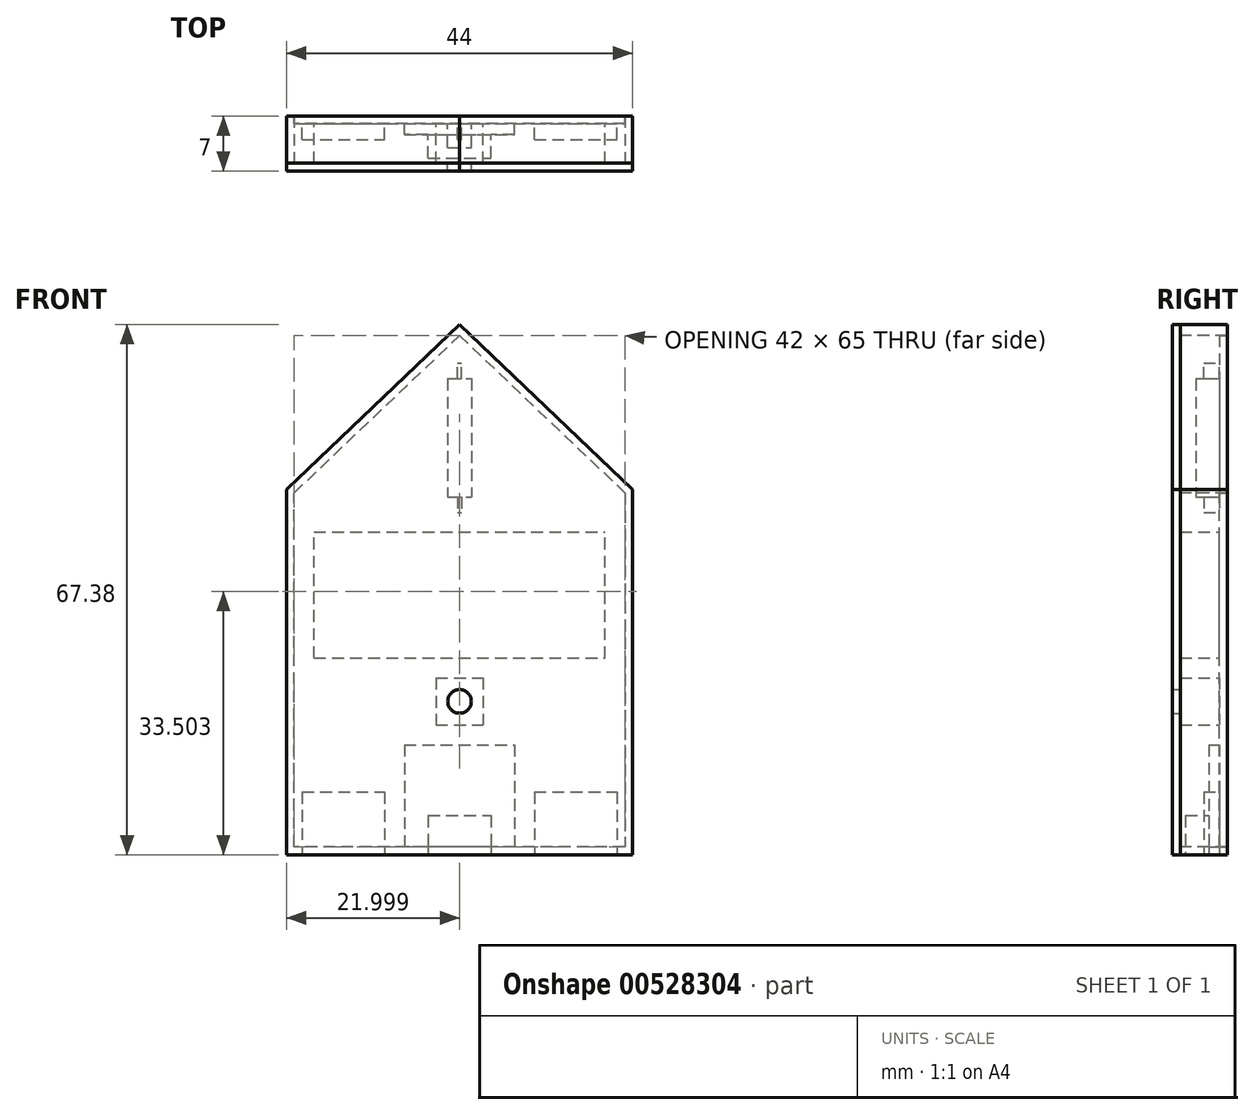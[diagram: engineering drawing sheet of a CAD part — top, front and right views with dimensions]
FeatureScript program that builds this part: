
annotation { "Feature Type Name" : "Feature", "Feature Type Description" : "" }
export const myFeature = defineFeature(function(context is Context, id is Id, definition is map)
    precondition{}
    {
        {
            var Q0;
            Q0=qCreatedBy(makeId("Front.planeOp"),FACE);
            var sketch = newSketch(context, id + "F0", { "sketchPlane" : qUnion([Q0])});
            skLineSegment(sketch, "E0", {"start": v(0.06, 2.74) * mm, "end": v(0.06, 47.74) * mm});
            skLineSegment(sketch, "E1", {"start": v(0.06, 47.74) * mm, "end": v(21.06, 67.74) * mm});
            skLineSegment(sketch, "E2", {"start": v(21.06, 67.74) * mm, "end": v(42.06, 47.74) * mm});
            skLineSegment(sketch, "E3", {"start": v(42.06, 47.74) * mm, "end": v(42.06, 2.74) * mm});
            skLineSegment(sketch, "E4", {"start": v(42.06, 2.74) * mm, "end": v(0.06, 2.74) * mm});
            skLineSegment(sketch, "E5", {"start": v(0.06, 47.74) * mm, "end": v(42.06, 47.74) * mm, "construction": true});
            skLineSegment(sketch, "E6", {"start": v(21.06, 67.74) * mm, "end": v(21.06, 47.74) * mm, "construction": true});
            skSolve(sketch);
        }
        {
            var Q0;
            Q0 = qSketchRegion(id + "F0", true);
            extrude(context, id + "F1", {"entities" : qUnion([Q0]), "depth" : 1 * mm, "offsetDistance" : 25 * mm});
        }
        {
            var Q0;
            Q0=makeQuery(id+"F1.opExtrude","CAP_FACE",FACE,{"disambiguationData":[OSD([sQuery(id+"F0.wireOp",EDGE,"E0"),sQuery(id+"F0.wireOp",EDGE,"E1"),sQuery(id+"F0.wireOp",EDGE,"E2"),sQuery(id+"F0.wireOp",EDGE,"E3"),sQuery(id+"F0.wireOp",EDGE,"E4")])],"isStart":false});
            var sketch = newSketch(context, id + "F2", { "sketchPlane" : qUnion([Q0])});
            skLineSegment(sketch, "E7.bottom", {"start": v(14.06, 15.74) * mm, "end": v(28.06, 15.74) * mm});
            skLineSegment(sketch, "E7.top", {"start": v(14.06, 2.74) * mm, "end": v(28.06, 2.74) * mm});
            skLineSegment(sketch, "E7.left", {"start": v(14.06, 15.74) * mm, "end": v(14.06, 2.74) * mm});
            skLineSegment(sketch, "E7.right", {"start": v(28.06, 15.74) * mm, "end": v(28.06, 2.74) * mm});
            skLineSegment(sketch, "E8", {"start": v(21.06, 15.74) * mm, "end": v(21.06, 2.74) * mm, "construction": true});
            skSolve(sketch);
        }
        {
            var Q0;
            Q0 = qSketchRegion(id + "F2", true);
            extrude(context, id + "F3", {"entities" : qUnion([Q0]), "depth" : 1.34 * mm, "offsetDistance" : 25 * mm});
        }
        {
            var Q0;
            Q0=makeQuery(id+"F3.opExtrude","CAP_FACE",FACE,{"disambiguationData":[OSD([sQuery(id+"F2.wireOp",EDGE,"E7.bottom"),sQuery(id+"F2.wireOp",EDGE,"E7.top"),sQuery(id+"F2.wireOp",EDGE,"E7.left"),sQuery(id+"F2.wireOp",EDGE,"E7.right")])],"isStart":false});
            var sketch = newSketch(context, id + "F4", { "sketchPlane" : qUnion([Q0])});
            skLineSegment(sketch, "E9.bottom", {"start": v(17.06, 6.74) * mm, "end": v(25.06, 6.74) * mm});
            skLineSegment(sketch, "E9.top", {"start": v(17.06, 1.74) * mm, "end": v(25.06, 1.74) * mm});
            skLineSegment(sketch, "E9.left", {"start": v(17.06, 6.74) * mm, "end": v(17.06, 1.74) * mm});
            skLineSegment(sketch, "E9.right", {"start": v(25.06, 6.74) * mm, "end": v(25.06, 1.74) * mm});
            skLineSegment(sketch, "E10", {"start": v(21.06, 6.74) * mm, "end": v(21.06, 1.74) * mm, "construction": true});
            skSolve(sketch);
        }
        {
            var Q0;
            Q0 = qSketchRegion(id + "F4", true);
            extrude(context, id + "F5", {"entities" : qUnion([Q0]), "operationType" : NewBodyOperationType.ADD, "depth" : 3 * mm, "offsetDistance" : 25 * mm});
        }
        {
            var Q0;
            Q0=makeQuery(id+"F2.imprint","IMPRINT",FACE,{"disambiguationData":[TD([[makeQuery(id+"F2.imprint","IMPRINT",EDGE,{"derivedFrom":sQuery(id+"F2.wireOp",EDGE,"E7.bottom")}),1.0]])]});
            var sketch = newSketch(context, id + "F6", { "sketchPlane" : qUnion([Q0])});
            skLineSegment(sketch, "E11.bottom", {"start": v(1.06, 9.74) * mm, "end": v(11.56, 9.74) * mm});
            skLineSegment(sketch, "E11.top", {"start": v(1.06, 1.74) * mm, "end": v(11.56, 1.74) * mm});
            skLineSegment(sketch, "E11.left", {"start": v(1.06, 9.74) * mm, "end": v(1.06, 1.74) * mm});
            skLineSegment(sketch, "E11.right", {"start": v(11.56, 9.74) * mm, "end": v(11.56, 1.74) * mm});
            skLineSegment(sketch, "E12.bottom", {"start": v(30.56, 9.74) * mm, "end": v(41.06, 9.74) * mm});
            skLineSegment(sketch, "E12.top", {"start": v(30.56, 1.74) * mm, "end": v(41.06, 1.74) * mm});
            skLineSegment(sketch, "E12.left", {"start": v(30.56, 9.74) * mm, "end": v(30.56, 1.74) * mm});
            skLineSegment(sketch, "E12.right", {"start": v(41.06, 9.74) * mm, "end": v(41.06, 1.74) * mm});
            skSolve(sketch);
        }
        {
            var Q0;
            Q0 = qSketchRegion(id + "F6", true);
            extrude(context, id + "F7", {"entities" : qUnion([Q0]), "depth" : 2 * mm, "offsetDistance" : 25 * mm});
        }
        {
            var Q0;
            Q0=makeQuery(id+"F2.imprint","IMPRINT",FACE,{"disambiguationData":[TD([[makeQuery(id+"F2.imprint","IMPRINT",EDGE,{"derivedFrom":sQuery(id+"F2.wireOp",EDGE,"E7.bottom")}),1.0]])]});
            var sketch = newSketch(context, id + "F8", { "sketchPlane" : qUnion([Q0])});
            skLineSegment(sketch, "E13.bottom", {"start": v(18.06, 24.24) * mm, "end": v(24.06, 24.24) * mm});
            skLineSegment(sketch, "E13.top", {"start": v(18.06, 18.24) * mm, "end": v(24.06, 18.24) * mm});
            skLineSegment(sketch, "E13.left", {"start": v(18.06, 24.24) * mm, "end": v(18.06, 18.24) * mm});
            skLineSegment(sketch, "E13.right", {"start": v(24.06, 24.24) * mm, "end": v(24.06, 18.24) * mm});
            skLineSegment(sketch, "E14", {"start": v(21.06, 24.24) * mm, "end": v(21.06, 18.24) * mm, "construction": true});
            skSolve(sketch);
        }
        {
            var Q0;
            Q0 = qSketchRegion(id + "F8", true);
            extrude(context, id + "F9", {"entities" : qUnion([Q0]), "depth" : 5 * mm, "offsetDistance" : 25 * mm});
        }
        {
            var Q0;
            Q0=makeQuery(id+"F9.opExtrude","CAP_FACE",FACE,{"disambiguationData":[OSD([sQuery(id+"F8.wireOp",EDGE,"E13.bottom"),sQuery(id+"F8.wireOp",EDGE,"E13.top"),sQuery(id+"F8.wireOp",EDGE,"E13.left"),sQuery(id+"F8.wireOp",EDGE,"E13.right")])],"isStart":false});
            var sketch = newSketch(context, id + "F10", { "sketchPlane" : qUnion([Q0])});
            skCircle(sketch, "E15", {"center": v(21.06, 21.24) * mm, "radius": 1.5 * mm});
            skLineSegment(sketch, "E16", {"start": v(18.06, 24.24) * mm, "end": v(24.06, 18.24) * mm, "construction": true});
            skLineSegment(sketch, "E17", {"start": v(24.06, 24.24) * mm, "end": v(18.06, 18.24) * mm, "construction": true});
            skSolve(sketch);
        }
        {
            var Q0;
            Q0 = qSketchRegion(id + "F10", true);
            extrude(context, id + "F11", {"entities" : qUnion([Q0]), "operationType" : NewBodyOperationType.ADD, "depth" : 1 * mm, "offsetDistance" : 25 * mm});
        }
        {
            var Q0;
            Q0=makeQuery(id+"F2.imprint","IMPRINT",FACE,{"disambiguationData":[TD([[makeQuery(id+"F2.imprint","IMPRINT",EDGE,{"derivedFrom":sQuery(id+"F2.wireOp",EDGE,"E7.bottom")}),1.0]])]});
            var sketch = newSketch(context, id + "F12", { "sketchPlane" : qUnion([Q0])});
            skLineSegment(sketch, "E18.bottom", {"start": v(2.56, 26.74) * mm, "end": v(39.56, 26.74) * mm});
            skLineSegment(sketch, "E18.top", {"start": v(2.56, 42.74) * mm, "end": v(39.56, 42.74) * mm});
            skLineSegment(sketch, "E18.left", {"start": v(2.56, 26.74) * mm, "end": v(2.56, 42.74) * mm});
            skLineSegment(sketch, "E18.right", {"start": v(39.56, 26.74) * mm, "end": v(39.56, 42.74) * mm});
            skLineSegment(sketch, "E19", {"start": v(21.06, 26.74) * mm, "end": v(21.06, 42.74) * mm, "construction": true});
            skSolve(sketch);
        }
        {
            var Q0;
            Q0 = qSketchRegion(id + "F12", true);
            extrude(context, id + "F13", {"entities" : qUnion([Q0]), "depth" : 5 * mm, "offsetDistance" : 25 * mm});
        }
        {
            var Q0;
            Q0=makeQuery(id+"F2.imprint","IMPRINT",FACE,{"disambiguationData":[TD([[makeQuery(id+"F2.imprint","IMPRINT",EDGE,{"derivedFrom":sQuery(id+"F2.wireOp",EDGE,"E7.bottom")}),1.0]])]});
            var sketch = newSketch(context, id + "F14", { "sketchPlane" : qUnion([Q0])});
            skLineSegment(sketch, "E20.bottom", {"start": v(19.56, 62.24) * mm, "end": v(22.56, 62.24) * mm});
            skLineSegment(sketch, "E20.top", {"start": v(19.56, 47.24) * mm, "end": v(22.56, 47.24) * mm});
            skLineSegment(sketch, "E20.left", {"start": v(19.56, 62.24) * mm, "end": v(19.56, 47.24) * mm});
            skLineSegment(sketch, "E20.right", {"start": v(22.56, 62.24) * mm, "end": v(22.56, 47.24) * mm});
            skPoint(sketch, "E21", {"position": v(21.06, 62.24) * mm});
            skSolve(sketch);
        }
        {
            var Q0;
            Q0 = qSketchRegion(id + "F14", true);
            extrude(context, id + "F15", {"entities" : qUnion([Q0]), "depth" : 3 * mm, "offsetDistance" : 25 * mm});
        }
        {
            var Q0;
            Q0=makeQuery(id+"F2.imprint","IMPRINT",FACE,{"disambiguationData":[TD([[makeQuery(id+"F2.imprint","IMPRINT",EDGE,{"derivedFrom":sQuery(id+"F2.wireOp",EDGE,"E7.bottom")}),1.0]])]});
            var sketch = newSketch(context, id + "F16", { "sketchPlane" : qUnion([Q0])});
            skLineSegment(sketch, "E22.bottom", {"start": v(20.8, 47.24) * mm, "end": v(21.3, 47.24) * mm});
            skLineSegment(sketch, "E22.top", {"start": v(20.8, 45.24) * mm, "end": v(21.3, 45.24) * mm});
            skLineSegment(sketch, "E22.left", {"start": v(20.8, 47.24) * mm, "end": v(20.8, 45.24) * mm});
            skLineSegment(sketch, "E22.right", {"start": v(21.3, 47.24) * mm, "end": v(21.3, 45.24) * mm});
            skLineSegment(sketch, "E23.bottom", {"start": v(20.8, 62.24) * mm, "end": v(21.3, 62.24) * mm});
            skLineSegment(sketch, "E23.top", {"start": v(20.8, 64.24) * mm, "end": v(21.3, 64.24) * mm});
            skLineSegment(sketch, "E23.left", {"start": v(20.8, 62.24) * mm, "end": v(20.8, 64.24) * mm});
            skLineSegment(sketch, "E23.right", {"start": v(21.3, 62.24) * mm, "end": v(21.3, 64.24) * mm});
            skPoint(sketch, "E24", {"position": v(21.06, 62.24) * mm});
            skSolve(sketch);
        }
        {
            var Q0;
            Q0 = qSketchRegion(id + "F16", true);
            extrude(context, id + "F17", {"entities" : qUnion([Q0]), "depth" : 2 * mm, "offsetDistance" : 25 * mm});
        }
        {
            var Q0;
            Q0=makeQuery(id+"F13.opExtrude","CAP_FACE",FACE,{"disambiguationData":[OSD([sQuery(id+"F12.wireOp",EDGE,"E18.bottom"),sQuery(id+"F12.wireOp",EDGE,"E18.top"),sQuery(id+"F12.wireOp",EDGE,"E18.left"),sQuery(id+"F12.wireOp",EDGE,"E18.right")])],"isStart":false});
            var sketch = newSketch(context, id + "F18", { "sketchPlane" : qUnion([Q0])});
            skSolve(sketch);
        }
        {
            var Q0;
            Q0=makeQuery(id+"F18.imprint","IMPRINT",FACE,{"disambiguationData":[TD([[makeQuery(id+"F18.imprint","IMPRINT",EDGE,{"derivedFrom":makeQuery(id+"F13.opExtrude","CAP_EDGE",EDGE,{"disambiguationData":[OSD([sQuery(id+"F12.wireOp",EDGE,"E18.bottom")])],"isStart":false})}),1.0]])]});
            var sketch = newSketch(context, id + "F19", { "sketchPlane" : qUnion([Q0])});
            skLineSegment(sketch, "E25.0", {"start": v(43.06, 1.74) * mm, "end": v(43.06, 48.17) * mm});
            skLineSegment(sketch, "E25.1", {"start": v(-0.94, 1.74) * mm, "end": v(43.06, 1.74) * mm});
            skLineSegment(sketch, "E25.2", {"start": v(43.06, 48.17) * mm, "end": v(21.06, 69.12) * mm});
            skLineSegment(sketch, "E25.3", {"start": v(21.06, 69.12) * mm, "end": v(-0.94, 48.17) * mm});
            skLineSegment(sketch, "E25.4", {"start": v(-0.94, 48.17) * mm, "end": v(-0.94, 1.74) * mm});
            skSolve(sketch);
        }
        {
            var Q0;
            Q0 = qSketchRegion(id + "F19", true);
            extrude(context, id + "F20", {"entities" : qUnion([Q0]), "depth" : 1 * mm, "offsetDistance" : 25 * mm});
        }
        {
            var Q0;
            Q0=makeQuery(id+"F20.opExtrude","CAP_FACE",FACE,{"disambiguationData":[OSD([sQuery(id+"F19.wireOp",EDGE,"E25.0"),sQuery(id+"F19.wireOp",EDGE,"E25.1"),sQuery(id+"F19.wireOp",EDGE,"E25.2"),sQuery(id+"F19.wireOp",EDGE,"E25.3"),sQuery(id+"F19.wireOp",EDGE,"E25.4")])],"isStart":true});
            var sketch = newSketch(context, id + "F21", { "sketchPlane" : qUnion([Q0])});
            skLineSegment(sketch, "E26.0.0", {"start": v(0.94, 48.17) * mm, "end": v(-21.06, 69.12) * mm});
            skLineSegment(sketch, "E26.0.1", {"start": v(-21.06, 69.12) * mm, "end": v(-43.06, 48.17) * mm});
            skLineSegment(sketch, "E26.0.2", {"start": v(-43.06, 48.17) * mm, "end": v(-43.06, 1.74) * mm});
            skLineSegment(sketch, "E26.0.3", {"start": v(-43.06, 1.74) * mm, "end": v(0.94, 1.74) * mm});
            skLineSegment(sketch, "E26.0.4", {"start": v(0.94, 1.74) * mm, "end": v(0.94, 48.17) * mm});
            skLineSegment(sketch, "E27.0", {"start": v(-21.06, 67.74) * mm, "end": v(-42.06, 47.74) * mm});
            skLineSegment(sketch, "E27.1", {"start": v(-0.06, 47.74) * mm, "end": v(-21.06, 67.74) * mm});
            skLineSegment(sketch, "E27.2", {"start": v(-42.06, 47.74) * mm, "end": v(-42.06, 2.74) * mm});
            skLineSegment(sketch, "E27.3", {"start": v(-42.06, 2.74) * mm, "end": v(-0.06, 2.74) * mm});
            skLineSegment(sketch, "E27.4", {"start": v(-0.06, 2.74) * mm, "end": v(-0.06, 47.74) * mm});
            skSolve(sketch);
        }
        {
            var Q0;
            Q0 = qSketchRegion(id + "F21", true);
            var Q1;
            Q1=makeQuery(id+"F1.opExtrude","CAP_FACE",FACE,{"disambiguationData":[OSD([sQuery(id+"F0.wireOp",EDGE,"E0"),sQuery(id+"F0.wireOp",EDGE,"E1"),sQuery(id+"F0.wireOp",EDGE,"E2"),sQuery(id+"F0.wireOp",EDGE,"E3"),sQuery(id+"F0.wireOp",EDGE,"E4")])],"isStart":true});
            extrude(context, id + "F22", {"entities" : qUnion([Q0]), "endBound" : BoundingType.UP_TO_SURFACE, "depth" : 25 * mm, "endBoundEntityFace" : qUnion([Q1]), "offsetDistance" : 25 * mm});
        }
    });
